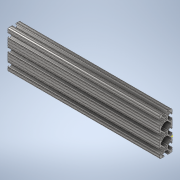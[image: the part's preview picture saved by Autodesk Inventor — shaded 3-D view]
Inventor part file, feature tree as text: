
AUTODESK INVENTOR PART (.ipt)
format: ipt  version: 2020 (Build 240168000, 168)  size: 378,368 bytes
history: native  units: in
note: dims shown in document units (in); Inventor stores cm internally (conversion verified against a paired STEP export)
features: sketch x2, extrude x1
ambient origin geometry x8: Origin, YZ Plane, XZ Plane, XY Plane, X Axis, Y Axis, Z Axis, Center Point
bodies: Solid1 (feature_tree)
feature tree (3):
  extrude  "Extrusion1"  [1 undecoded]
  sketch  "Sketch2"
  sketch  "Sketch1"  dims[d0=12.0in d1=0.0in]
note: 1 required parameter value undecoded (feature->parameter linkage not recoverable at this tier; creation-order binding heuristic only, values carry confidence <= 0.55)
